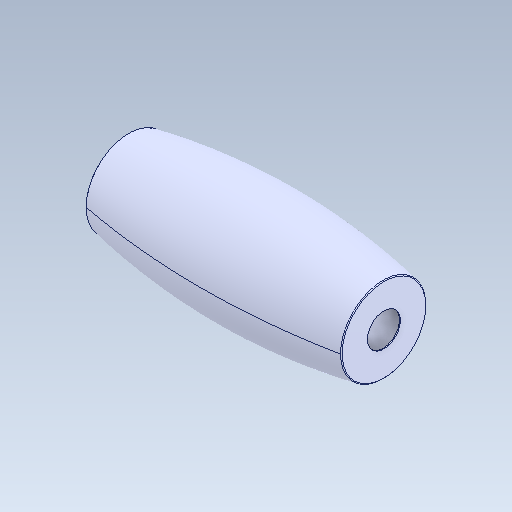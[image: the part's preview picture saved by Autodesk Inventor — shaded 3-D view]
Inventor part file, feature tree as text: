
AUTODESK INVENTOR PART (.ipt)
format: ipt  version: 2020.2 (Build 242310000, 310)  size: 163,328 bytes
history: native  units: in
note: dims shown in document units (in); Inventor stores cm internally (conversion verified against a paired STEP export)
features: fillet x1
ambient origin geometry x8: Origin, YZ Plane, XZ Plane, XY Plane, X Axis, Y Axis, Z Axis, Center Point
bodies: Solid1 (feature_tree)
feature tree (1):
  fillet  "Fillet1"  [1 undecoded]
note: 1 required parameter value undecoded (feature->parameter linkage not recoverable at this tier; creation-order binding heuristic only, values carry confidence <= 0.55)
